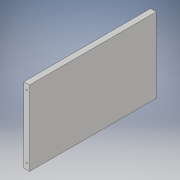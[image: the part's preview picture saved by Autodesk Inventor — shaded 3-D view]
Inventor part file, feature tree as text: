
AUTODESK INVENTOR PART (.ipt)
format: ipt  version: 2018 (Build 220112000, 112)  size: 101,376 bytes
history: native  units: in
note: dims shown in document units (in); Inventor stores cm internally (conversion verified against a paired STEP export)
features: sketch x2, extrude x2
ambient origin geometry x8: Origin, YZ Plane, XZ Plane, XY Plane, X Axis, Y Axis, Z Axis, Center Point
bodies: Body1 (feature_tree)
feature tree (4):
  sketch  "Sketch2"  dims[d0=13.0in d1=22.0in]
  extrude  "Extrusion2"  Depth=22.0in
  extrude  "Extrusion4"  Depth=1.0in TaperAngle=0.0deg
  sketch  "Sketch4"  dims[d6=1.0in d7=0.0in d15=36.0in d16=0.0in d17=1.0in d18=0.2031in d19=11.0in d20=0.2031in]
